# Revit family: BC ACS IN_BAXI
name_source: partatom
category: Equipos mecánicos
units: mm (PartAtom-declared; Revit-internal decimal feet)

## family parameters
Compartido = No
Corte con vacíos al cargar = No
Cota de conector redondo = Diámetro de uso
Número OmniClass = 23.75.10.11.14
Punto de cálculo de habitación = No
Se basa en plano de trabajo = No
Siempre vertical = Sí
Tipo de pieza = Normal
Título OmniClass = Hot Water Heat Generators

## types (2) — shared parameters
Anchura = 690 mm
Angulo = 60.00°
Angulo 2 = 50.00°
Azul = Color RGB 002-061-157
Blanco = Color RAL 9016
Cap Altura = 400 mm  [stored 1.31234 ft]
Cap Altura Compensacion = 420 mm  [stored 1.37795 ft]
Cap Diametro = 640 mm  [stored 2.09974 ft]
Cap Diametro Compensacion = 680 mm  [stored 2.23097 ft]
DCW Distancia = 90 mm
Descripción = BC ACS IN
Diamentro Extraccion Aire = 200 mm  [stored 0.656168 ft]
Diametro = 600 mm
Diametro Agua Caliente = 19 mm  [stored 0.062336 ft]
Diametro Agua Fria = 19 mm  [stored 0.062336 ft]
Diametro Entrada Aire = 200 mm  [stored 0.656168 ft]
Distancia Conducto 1 = 217 mm  [stored 0.711942 ft]
Drenaje = 16 mm  [stored 0.0524934 ft]
Fabricante = BAXI
Gris = Color RAL 9006
Hielo = Color RGB 218-227-224
IFCExportAs = IfcBoilerType
Longitud = 697 mm
Negro = Color RGB 045-045-045
Potencia Electrica abs. = 500 W
Rad = 318 mm
Revit Version = 2016
Rojo = Color RGB 198-000-000
Tipo Categoria Tub. = M561
URL = https://www.baxi.es
URL PRODUCTO = https://www.baxi.es
Usar diametro nominal = Sí
Verde = Color RGB 106-158-058
Voltage = 230 V

## per-type parameters (varying)
| type | Altura | Altura Area Mantenimiento | Código de montaje | DHW Distancia | Distancia Drenaje | H | Modelo | Tipo Articulo | Volumen |
| BC ACS 200 IN | 1690 mm | 1690 mm | 144300002 | 974 mm | 1280 mm | 1270 mm | 200 IN | 200 IN | 215.0 L |
| BC ACS 300 IN | 2000 mm  [stored 6.56168 ft] | 2000 mm  [stored 6.56168 ft] | 144300000 | 1287 mm  [stored 4.22244 ft] | 1590 mm  [stored 5.21654 ft] | 1580 mm  [stored 5.18373 ft] | 300 IN | 300 IN | 270.0 L |

note: [stored X ft] marks values corroborated as IEEE doubles in the binary element streams (Revit-internal decimal feet)

## geometry (parser evidence)
native form markers: Sweep x2
no freeform markers — native parametric forms only
